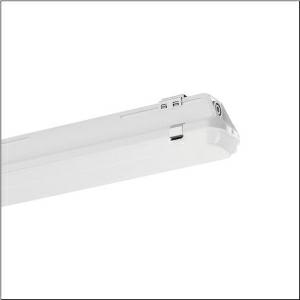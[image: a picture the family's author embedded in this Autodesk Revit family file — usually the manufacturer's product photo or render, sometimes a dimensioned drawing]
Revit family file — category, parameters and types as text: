
# Revit family: monsun_r__11_emergency_51fp207p467l3g_034d
name_source: partatom
category: Lighting Fixtures
units: mm (PartAtom-declared; Revit-internal decimal feet)

## family parameters
Cut with Voids When Loaded = No
Host = Face
Light Source = No
Part Type = Normal
Room Calculation Point = No
Round Connector Dimension = Use Diameter
Shared = No

## types (1)
- --- (1 x LED, 890 lm, 6.5 W, 4000K)
    Apparent Load = 7 VA
    CIE Flux Codes = 45 75 93 94 100
    Color Rendering = 80
    Color Temperature = 4000K
    Default Elevation = 1800 mm
    Description = Monsun® 11 emergency, damp-proof luminaire, chain hanger, primary optical cover: enclosure, of PC, light emission: direct distribution, primary light characteristic: symmetric, installation type: suspended mounting, surface-mounted, horizontal mounting, vertical mounting, LED, rated luminous flux: 5.450lm, luminous efficacy: 161lm/W, light colour: 840, colour temperature: 4000K, control gear: ON/OFF, with terminal, 4-pole, max. 2.5mm², mains connection: 220..240V, AC, 50/60Hz, rated input power: 37W, control gear: single battery element, battery: LiFePO4, 9Ah, luminaire housing, of glass-fibre reinforced polyester, uncoated, bright grey, incl. chain hanger, length: 1.590mm, width: 90mm, height: 88mm, clip for enclosure, of stainless steel (V2A), ceiling mounting element, of stainless steel (V2A), chain hanger, of stainless steel (V2A), protection rating (complete): IP66, insulation class (complete): insulation class I (protective earthing), certification: CE, UKCA, protection symbol: D, impact resistance: IK08, permissible operating ambient temperature: +5..+35°C, standard: EN 50419, EN 60598-2-1, EN 60598-2-22, contact your sales advisor before using the luminaires in applications with unclear chemical exposure, large temperature fluctuations or condensation-forming humidity, LABS conformity tested according to VDMA 24364:2018-05, no direct snow, no direct sun, no direct rain, for indoor or canopied outdoor use, corresponds to IFS (International Featured Standards) requirements for safety and quality in the food industry, packaging unit: 1 piece
    Height = 89 mm
    Lamp = 1 x LED
    Lamp Light Flux = 890 lm
    Lamp Power = 6.5 W
    Lamp count = 1
    Length = 1590 mm
    Luminous efficacy = 137 lm/W
    Manufacturer = Siteco
    ModVariant = No
    Model = 51FP207P467L3G
    Mounting Place = Ceiling
    Mounting Type = Surface mounted
    Number of Poles = 1
    OnlyDefault = Yes
    Power Factor = 1
    Product Name = Monsun® 11 emergency
    Product group = damp-proof luminaire
    ProductGroupID = 300
    Protection Class = Protection class I
    Protection Degree = IP 66
    RLX_Detail_Level = 1
    RLX_Emergency_Light_Flux = 0 lm
    RLX_Emergency_Type = 0
    RLX_Emergency_Type_DB = No
    RlxData = <blob elided: 89165 chars, md5=bbae47b3>
    Socket = socket
    Standby Power = 0 W
    System Light Flux = 890 lm
    System Power = 7 W
    Type Comments = : emergency light operation: 3 h
    Type Image = l_1349237.jpg
    URL = http://relux.com
    VarID = @adj_018354
    Voltage = 0 V
    Weight = 0.00 kg
    Width = 90 mm

## geometry (parser evidence)
native form markers: Blend x4, Sweep x14
no freeform markers — native parametric forms only
